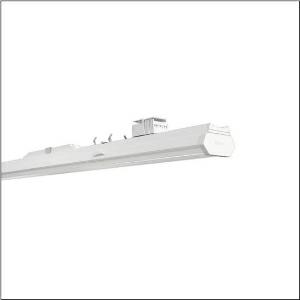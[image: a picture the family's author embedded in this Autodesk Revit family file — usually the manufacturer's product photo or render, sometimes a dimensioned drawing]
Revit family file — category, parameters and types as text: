
# Revit family: licross_r__11_protected_mo_51tp11cn48xfd_b8a8
name_source: partatom
category: Lighting Fixtures
units: mm (PartAtom-declared; Revit-internal decimal feet)

## family parameters
Cut with Voids When Loaded = No
Host = Face
Light Source = No
Part Type = Normal
Room Calculation Point = No
Round Connector Dimension = Use Diameter
Shared = No

## types (1)
- --- (1 x LED, 3300 lm, 22.1 W, 4000K)
    Apparent Load = 22 VA
    CIE Flux Codes = 83 94 98 100 100
    Color Rendering = 80
    Color Temperature = 4000K
    Default Elevation = 1800 mm
    Description = Licross® 11 Protected MOluminaire insert, length: 1.500mm, width: 90mm, height: 101mm, LED rated luminous flux: 8.140lm, light colour: 840, control gear: ON/OFF Multilumen, CLOi, control gear: ECG Multilumen, with plug, 6-pole, with phase selection, mains connection: 220..240V, AC/DC, 0/50..60Hz, without changeover relay, for emergency light function, for central battery installations according to DIN EN 60598-2-22, halogen-free wiring, primary optical cover: cover, of PMMA, light emission: direct with ceiling illumination distribution, protection rating (complete): IP64, insulation class (complete): insulation class I (protective earthing), certification: CE, ENEC, VDE, protection symbol: D if used in an environment without relevant dust loads with corresponding accessories, permissible ambient temperature for indoor applications: -35..+40°C, standard: EN 60598-2-22, reducing of maximum allowable ambient temperature of 5°C with ceiling mounting, corresponds to IFS (International Featured Standards) requirements for safety and quality in the food industry, packaging unit: 1 piece
    Height = 92 mm
    Lamp = 1 x LED
    Lamp Light Flux = 3300 lm
    Lamp Power = 22.1 W
    Lamp count = 1
    Length = 1500 mm
    Luminous efficacy = 149 lm/W
    Manufacturer = Siteco
    ModVariant = No
    Model = 51TP11CN48XFD
    Mounting Place = Ceiling
    Mounting Type = Pendant
    Number of Poles = 1
    OnlyDefault = Yes
    Power Factor = 1
    Product Name = Licross® 11 Protected MO
    Product group = luminaire insert
    ProductGroupID = 902
    Protection Class = Protection class I
    Protection Degree = IP 64
    RLX_Detail_Level = 1
    RlxData = <blob elided: 21921 chars, md5=57bcf722>
    Socket = socket
    Standby Power = 0 W
    System Light Flux = 3300 lm
    System Power = 22 W
    Type Comments = : DC mode (central or group accumulator) initial emergency light level
    Type Image = l_1256148.jpg
    URL = http://relux.com
    VarID = @adj_134587
    Voltage = 0 V
    Weight = 0.00 kg
    Width = 88 mm

## geometry (parser evidence)
native form markers: Blend x4, Sweep x10
no freeform markers — native parametric forms only
